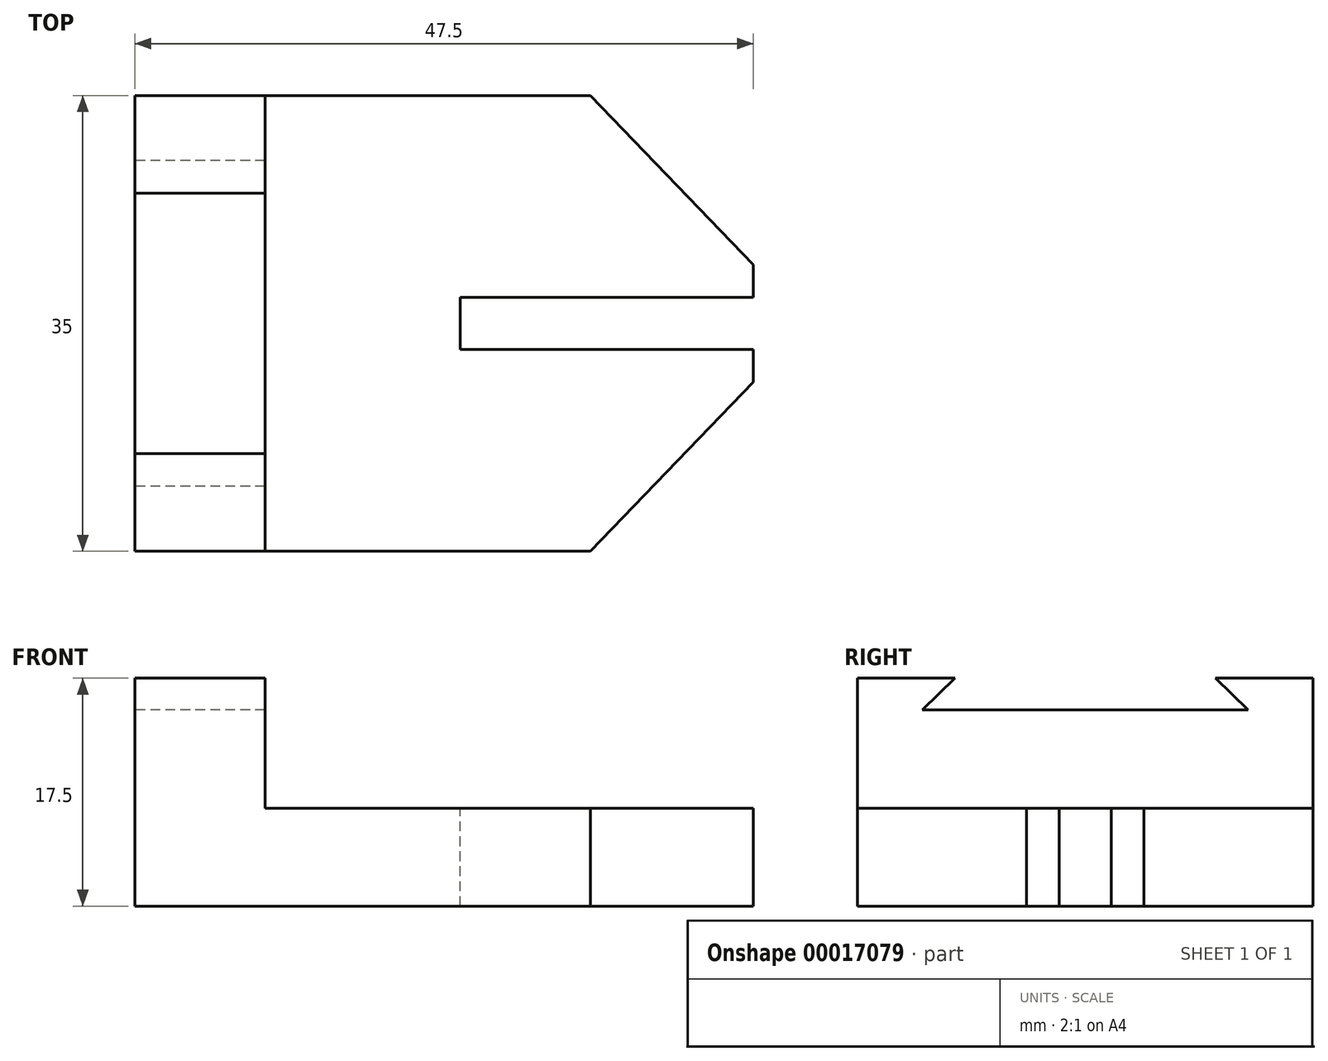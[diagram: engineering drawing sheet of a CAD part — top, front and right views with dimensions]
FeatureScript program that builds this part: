
annotation { "Feature Type Name" : "Feature", "Feature Type Description" : "" }
export const myFeature = defineFeature(function(context is Context, id is Id, definition is map)
    precondition{}
    {
        {
            var Q0;
            Q0=qCreatedBy(makeId("Right.planeOp"),FACE);
            var sketch = newSketch(context, id + "F0", { "sketchPlane" : qUnion([Q0])});
            skLineSegment(sketch, "E0", {"start": v(-15.28, 20.17) * mm, "end": v(-15.28, 2.67) * mm});
            skLineSegment(sketch, "E1", {"start": v(-15.28, 2.67) * mm, "end": v(19.72, 2.67) * mm});
            skLineSegment(sketch, "E2", {"start": v(19.72, 2.67) * mm, "end": v(19.72, 20.17) * mm});
            skLineSegment(sketch, "E3", {"start": v(19.72, 20.17) * mm, "end": v(12.22, 20.17) * mm});
            skLineSegment(sketch, "E4", {"start": v(12.22, 20.17) * mm, "end": v(14.72, 17.75) * mm});
            skLineSegment(sketch, "E5", {"start": v(14.72, 17.75) * mm, "end": v(-10.28, 17.75) * mm});
            skLineSegment(sketch, "E6", {"start": v(-10.28, 17.75) * mm, "end": v(-7.78, 20.17) * mm});
            skLineSegment(sketch, "E7", {"start": v(-7.78, 20.17) * mm, "end": v(-15.28, 20.17) * mm});
            skPoint(sketch, "E8", {"position": v(19.72, 10.17) * mm});
            skLineSegment(sketch, "E9", {"start": v(19.72, 10.17) * mm, "end": v(-15.28, 10.17) * mm});
            skSolve(sketch);
        }
        {
            var Q0;
            {var subQ2=sQuery(id+"F0.wireOp",EDGE,"E1");Q0=makeQuery(id+"F0.imprint","IMPRINT",FACE,{"disambiguationData":[TD([[makeQuery(id+"F0.imprint","IMPRINT",EDGE,{"derivedFrom":subQ2}),1.0]])]});}
            extrude(context, id + "F1", {"entities" : qUnion([Q0]), "depth" : 47.5 * mm});
        }
        {
            var Q0;
            {var subQ2=sQuery(id+"F0.wireOp",EDGE,"E3");Q0=makeQuery(id+"F0.imprint","IMPRINT",FACE,{"disambiguationData":[TD([[makeQuery(id+"F0.imprint","IMPRINT",EDGE,{"derivedFrom":subQ2}),1.0]])]});}
            extrude(context, id + "F2", {"entities" : qUnion([Q0]), "operationType" : NewBodyOperationType.ADD, "depth" : 10 * mm});
        }
        {
            var Q0;
            Q0=makeQuery(id+"F1.opExtrude","SWEPT_FACE",FACE,{"disambiguationData":[OSD([sQuery(id+"F0.wireOp",EDGE,"E9")])]});
            var sketch = newSketch(context, id + "F3", { "sketchPlane" : qUnion([Q0])});
            skPoint(sketch, "E10", {"position": v(35, -15.28) * mm});
            skPoint(sketch, "E11", {"position": v(47.5, -2.28) * mm});
            skPoint(sketch, "E12", {"position": v(47.5, 6.72) * mm});
            skPoint(sketch, "E13", {"position": v(35, 19.72) * mm});
            skPoint(sketch, "E14", {"position": v(47.5, 4.22) * mm});
            skPoint(sketch, "E15", {"position": v(43.28, -24.4) * mm});
            skPoint(sketch, "E16", {"position": v(47.5, 0.22) * mm});
            skLineSegment(sketch, "E17", {"start": v(47.5, 4.22) * mm, "end": v(25, 4.22) * mm});
            skLineSegment(sketch, "E18", {"start": v(25, 4.22) * mm, "end": v(25, 0.22) * mm});
            skLineSegment(sketch, "E19", {"start": v(25, 0.22) * mm, "end": v(47.5, 0.22) * mm});
            skLineSegment(sketch, "E20", {"start": v(35, -15.28) * mm, "end": v(47.5, -2.28) * mm});
            skLineSegment(sketch, "E21", {"start": v(35, 19.72) * mm, "end": v(47.5, 6.72) * mm});
            skLineSegment(sketch, "E22", {"start": v(47.5, 4.22) * mm, "end": v(47.5, 0.22) * mm});
            skSolve(sketch);
        }
        {
            var Q0;
            Q0=makeQuery(id+"F3.imprint","IMPRINT",FACE,{"disambiguationData":[TD([[makeQuery(id+"F3.imprint","IMPRINT",EDGE,{"derivedFrom":sQuery(id+"F3.wireOp",EDGE,"E17")}),1.0]])]});
            var Q1;
            {var subQ2=sQuery(id+"F3.wireOp",EDGE,"E21");Q1=makeQuery(id+"F3.imprint","IMPRINT",FACE,{"disambiguationData":[TD([[makeQuery(id+"F3.imprint","IMPRINT",EDGE,{"derivedFrom":subQ2}),1.0]])]});}
            var Q2;
            {var subQ2=sQuery(id+"F3.wireOp",EDGE,"E20");Q2=makeQuery(id+"F3.imprint","IMPRINT",FACE,{"disambiguationData":[TD([[makeQuery(id+"F3.imprint","IMPRINT",EDGE,{"derivedFrom":subQ2}),-1.0]])]});}
            extrude(context, id + "F4", {"entities" : qUnion([Q0, Q1, Q2]), "operationType" : NewBodyOperationType.REMOVE, "endBound" : BoundingType.THROUGH_ALL, "oppositeDirection" : true, "depth" : 25 * mm});
        }
    });
